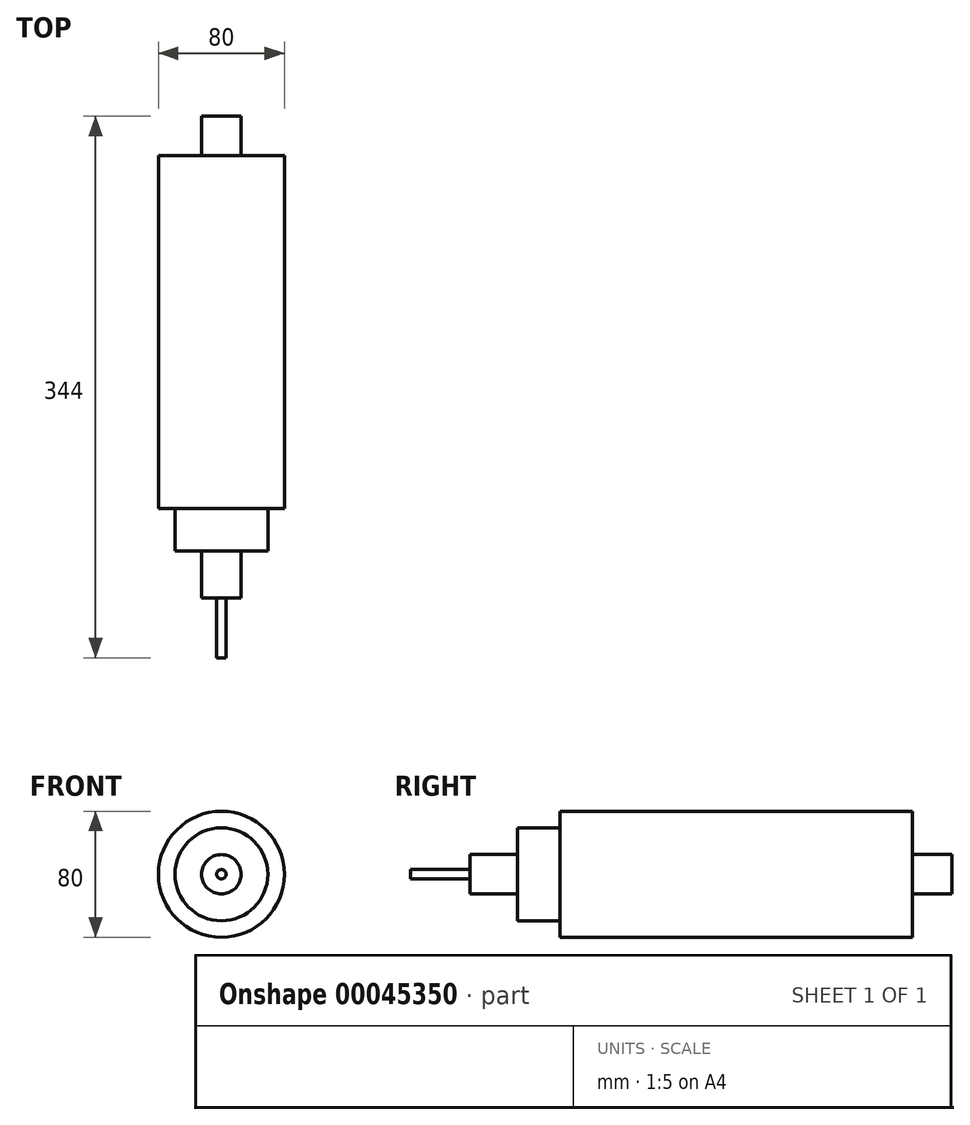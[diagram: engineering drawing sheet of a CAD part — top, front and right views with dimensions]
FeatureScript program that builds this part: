
annotation { "Feature Type Name" : "Feature", "Feature Type Description" : "" }
export const myFeature = defineFeature(function(context is Context, id is Id, definition is map)
    precondition{}
    {
        {
            var Q0;
            Q0=qCreatedBy(makeId("Front.planeOp"),FACE);
            var sketch = newSketch(context, id + "F0", { "sketchPlane" : qUnion([Q0])});
            skCircle(sketch, "E0", {"center": v(0, 0) * mm, "radius": 40 * mm});
            skSolve(sketch);
        }
        {
            var Q0;
            Q0 = qSketchRegion(id + "F0", true);
            extrude(context, id + "F1", {"entities" : qUnion([Q0]), "depth" : 224 * mm});
        }
        {
            var Q0;
            Q0=makeQuery(id+"F1.opExtrude","CAP_FACE",FACE,{"disambiguationData":[OSD([sQuery(id+"F0.wireOp",EDGE,"E0")])],"isStart":false});
            var sketch = newSketch(context, id + "F2", { "sketchPlane" : qUnion([Q0])});
            skCircle(sketch, "E1", {"center": v(0, 0) * mm, "radius": 29.5 * mm});
            skSolve(sketch);
        }
        {
            var Q0;
            Q0 = qSketchRegion(id + "F2", true);
            extrude(context, id + "F3", {"entities" : qUnion([Q0]), "operationType" : NewBodyOperationType.ADD, "depth" : 27 * mm});
        }
        {
            var Q0;
            Q0=makeQuery(id+"F3.opExtrude","CAP_FACE",FACE,{"disambiguationData":[OSD([sQuery(id+"F2.wireOp",EDGE,"E1")])],"isStart":false});
            var sketch = newSketch(context, id + "F4", { "sketchPlane" : qUnion([Q0])});
            skCircle(sketch, "E2", {"center": v(0, 0) * mm, "radius": 12.5 * mm});
            skSolve(sketch);
        }
        {
            var Q0;
            Q0 = qSketchRegion(id + "F4", true);
            extrude(context, id + "F5", {"entities" : qUnion([Q0]), "operationType" : NewBodyOperationType.ADD, "depth" : 30 * mm});
        }
        {
            var Q0;
            Q0=makeQuery(id+"F1.opExtrude","CAP_FACE",FACE,{"disambiguationData":[OSD([sQuery(id+"F0.wireOp",EDGE,"E0")])],"isStart":true});
            var sketch = newSketch(context, id + "F6", { "sketchPlane" : qUnion([Q0])});
            skCircle(sketch, "E3", {"center": v(0, 0) * mm, "radius": 12.5 * mm});
            skSolve(sketch);
        }
        {
            var Q0;
            Q0 = qSketchRegion(id + "F6", true);
            extrude(context, id + "F7", {"entities" : qUnion([Q0]), "operationType" : NewBodyOperationType.ADD, "depth" : 25 * mm});
        }
        {
            var Q0;
            Q0=makeQuery(id+"F5.opExtrude","CAP_FACE",FACE,{"disambiguationData":[OSD([sQuery(id+"F4.wireOp",EDGE,"E2")])],"isStart":false});
            var sketch = newSketch(context, id + "F8", { "sketchPlane" : qUnion([Q0])});
            skCircle(sketch, "E4", {"center": v(0, 0) * mm, "radius": 3 * mm});
            skSolve(sketch);
        }
        {
            var Q0;
            Q0 = qSketchRegion(id + "F8", true);
            extrude(context, id + "F9", {"entities" : qUnion([Q0]), "operationType" : NewBodyOperationType.ADD, "depth" : 38 * mm});
        }
    });
